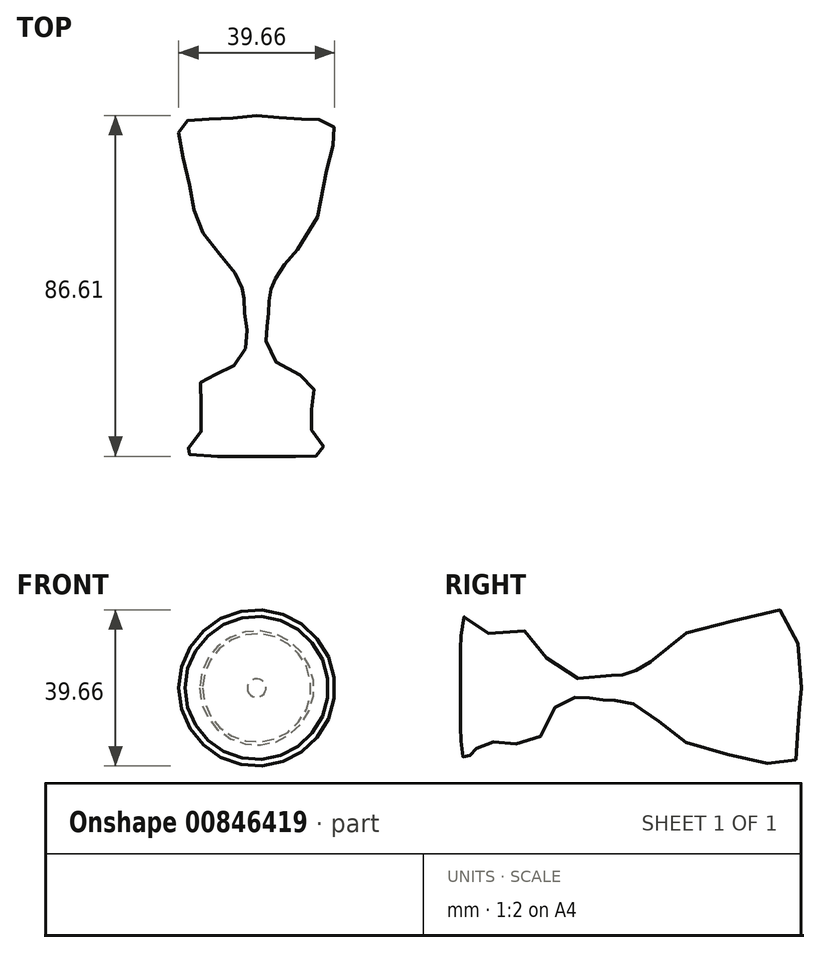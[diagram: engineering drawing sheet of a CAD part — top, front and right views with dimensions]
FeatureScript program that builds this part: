
annotation { "Feature Type Name" : "Feature", "Feature Type Description" : "" }
export const myFeature = defineFeature(function(context is Context, id is Id, definition is map)
    precondition{}
    {
        {
            var Q0;
            Q0=qCreatedBy(makeId("Top.planeOp"),FACE);
            var sketch = newSketch(context, id + "F0", { "sketchPlane" : qUnion([Q0])});
            skFitSpline(sketch, "E0", {"points": [v(0, 28.25) * mm, v(-12.06, 27.33) * mm, v(-19.4, 25.8) * mm, v(-17.56, 13.28) * mm, v(-14.5, 0) * mm, v(-5.95, -11.15) * mm, v(-3.51, -16.34) * mm, v(-3.2, -18.48) * mm, v(-2.9, -23.36) * mm, v(-2.6, -30.08) * mm, v(-8.1, -36.8) * mm, v(-14.2, -39.55) * mm, v(-14.2, -52.37) * mm, v(-18.17, -57.26) * mm, v(0, -58.18) * mm], "startDerivative": vector(-145.23, -15.8) * mm, "endDerivative": vector(265.29, 7.06) * mm});
            skLineSegment(sketch, "E1", {"start": v(0, 0) * mm, "end": v(0, 36.8) * mm});
            skLineSegment(sketch, "E2", {"start": v(0, 36.8) * mm, "end": v(0, -65.5) * mm});
            skSolve(sketch);
        }
        {
            var Q0;
            {var subQ0=sQuery(id+"F0.wireOp",EDGE,"E0");Q0=makeQuery(id+"F0.imprint","IMPRINT",FACE,{"disambiguationData":[TD([[makeQuery(id+"F0.imprint","IMPRINT",EDGE,{"derivedFrom":subQ0}),1.0]])]});}
            var Q1;
            Q1=sQuery(id+"F0.wireOp",EDGE,"E2");
            revolve(context, id + "F1", {"surfaceOperationType" : NewSurfaceOperationType.NEW, "entities" : qUnion([Q0]), "axis" : qUnion([Q1]), "revolveType" : RevolveType.FULL});
        }
    });
